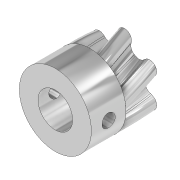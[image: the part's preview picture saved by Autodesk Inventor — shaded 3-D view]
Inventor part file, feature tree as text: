
AUTODESK INVENTOR PART (.ipt)
format: ipt  version: 2020 (Build 240168000, 168)  size: 375,296 bytes
history: native  units: in
note: dims shown in document units (in); Inventor stores cm internally (conversion verified against a paired STEP export)
features: sketch x5, extrude x2, sweep x1, other x1, projected_geometry x1
ambient origin geometry x8: Origin, YZ Plane, XZ Plane, XY Plane, X Axis, Y Axis, Z Axis, Center Point
bodies: Solid1 (feature_tree)
feature tree (10):
  sweep  "Sweep1"
  sketch  "3D Sketch2"
  extrude  "Extrusion1"  Depth=0.0787in
  extrude  "Extrusion2"  Depth=0.1969in
  sketch  "Sketch1"  dims[d0=0.1969in d1=0.4094in]
  sketch  "3D Sketch1"
  other  "Helical Curve1"
  sketch  "Sketch2"  dims[d2=0.0866in d3=0.0787in]
  projected_geometry  "Projected Loop1"
  sketch  "Sketch3"  dims[d4=0.0787in d5=0.0787in d6=2.3622in d8=360.0deg d10=0.1969in d11=0.0236in d12=0.236in d13=0.0in d14=0.0in d15=0.0in d16=0.1969in d17=0.0in d18=0.0748in d19=0.205in d20=0.0in]
